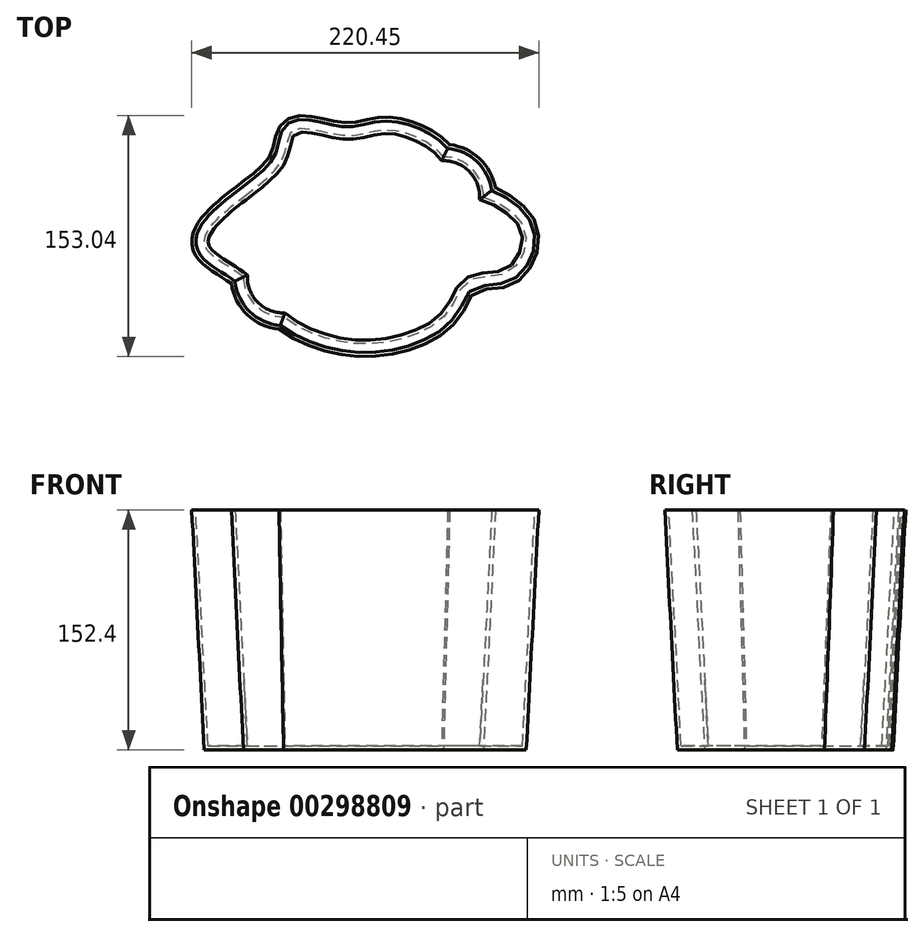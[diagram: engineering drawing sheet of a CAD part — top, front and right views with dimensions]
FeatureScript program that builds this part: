
annotation { "Feature Type Name" : "Feature", "Feature Type Description" : "" }
export const myFeature = defineFeature(function(context is Context, id is Id, definition is map)
    precondition{}
    {
        {
            var Q0;
            Q0=qCreatedBy(makeId("Top.planeOp"),FACE);
            var sketch = newSketch(context, id + "F0", { "sketchPlane" : qUnion([Q0])});
            skLineSegment(sketch, "E0.left", {"start": v(-76.08, 46.94) * mm, "end": v(-76.08, -3.86) * mm});
            skPoint(sketch, "E1.visualSharp", {"position": v(-76.08, 72.34) * mm});
            skPoint(sketch, "E2.visualSharp", {"position": v(76.32, 72.34) * mm});
            skArc(sketch, "E2.filletArc", {"start": v(76.32, 46.94) * mm, "mid": v(68.88, 64.9) * mm, "end": v(50.92, 72.34) * mm});
            skPoint(sketch, "E3.visualSharp", {"position": v(76.32, -29.26) * mm});
            skPoint(sketch, "E4.visualSharp", {"position": v(-76.08, -29.26) * mm});
            skArc(sketch, "E4.filletArc", {"start": v(-76.08, -3.86) * mm, "mid": v(-68.64, -21.82) * mm, "end": v(-50.68, -29.26) * mm});
            skFitSpline(sketch, "E5", {"points": [v(-76.08, 46.94) * mm, v(-50.68, 72.34) * mm, v(-43.91, 89.6) * mm, v(-10.35, 85.93) * mm, v(15.4, 89.6) * mm, v(50.92, 72.34) * mm, v(60, 52.36) * mm, v(76.32, 46.94) * mm, v(102.76, 25.24) * mm, v(93.56, 0) * mm, v(76.32, -3.86) * mm, v(63.68, -9.25) * mm, v(50.92, -29.26) * mm, v(0, -46.5) * mm, v(-50.68, -29.26) * mm, v(-76.08, -3.86) * mm, v(-100.92, 17.42) * mm, v(-76.08, 46.94) * mm]});
            skSolve(sketch);
        }
        {
            var Q0;
            Q0 = qSketchRegion(id + "F0", true);
            extrude(context, id + "F1", {"entities" : qUnion([Q0]), "depth" : 152.4 * mm, "hasDraft" : true, "draftAngle" : 3 * degree});
        }
        {
            var Q0;
            Q0=makeQuery(id+"F1.opExtrude","CAP_FACE",FACE,{"disambiguationData":[OSD([sQuery(id+"F0.wireOp",EDGE,"E2.filletArc"),sQuery(id+"F0.wireOp",EDGE,"E4.filletArc"),sQuery(id+"F0.wireOp",EDGE,"E5"),sQuery(id+"F0.wireOp",EDGE,"E5")])],"isStart":false});
            shell(context, id + "F2", {"entities" : qUnion([Q0]), "thickness" : 2.54 * mm});
        }
    });
